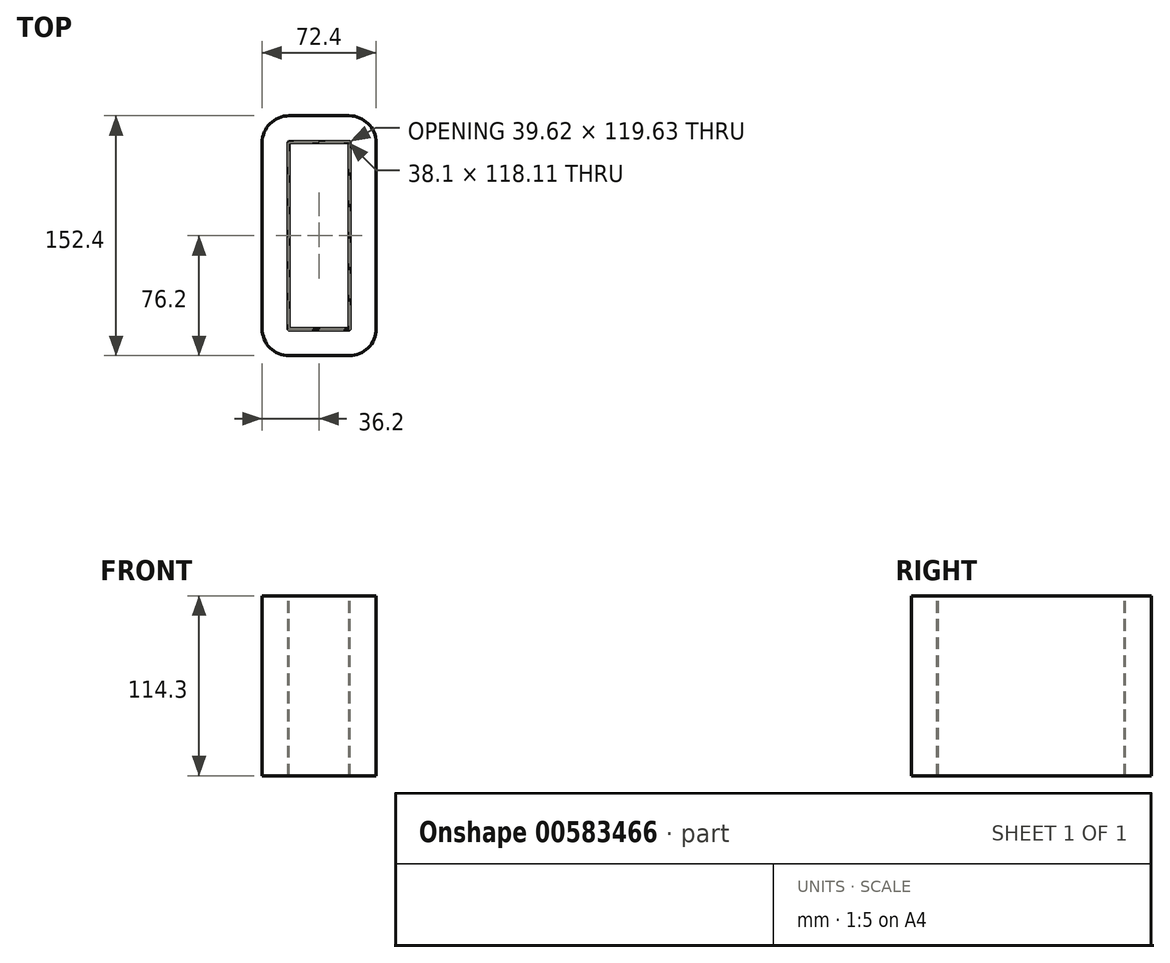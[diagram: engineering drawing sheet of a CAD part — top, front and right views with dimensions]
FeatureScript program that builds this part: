
annotation { "Feature Type Name" : "Feature", "Feature Type Description" : "" }
export const myFeature = defineFeature(function(context is Context, id is Id, definition is map)
    precondition{}
    {
        {
            assignVariable(context, id + "F0", {"name" : "Tongue", "anyValue" : 38.1 * mm});
        }
        {
            assignVariable(context, id + "F1", {"name" : "WindingWidth", "anyValue" : 114.3 * mm});
        }
        {
            assignVariable(context, id + "F2", {"name" : "CoilForm", "anyValue" : 0.76 * mm});
        }
        {
            assignVariable(context, id + "F3", {"name" : "CoilBuild", "anyValue" : 0.45 * getVariable(context, 'Tongue')});
        }
        {
            var Q0;
            Q0=qCreatedBy(makeId("Top.planeOp"),FACE);
            var sketch = newSketch(context, id + "F4", { "sketchPlane" : qUnion([Q0])});
            skLineSegment(sketch, "E0.bottom", {"start": v(-36.2, -76.2) * mm, "end": v(36.2, -76.2) * mm});
            skLineSegment(sketch, "E0.top", {"start": v(-36.2, 76.2) * mm, "end": v(36.2, 76.2) * mm});
            skLineSegment(sketch, "E0.left", {"start": v(-36.2, -76.2) * mm, "end": v(-36.2, 76.2) * mm});
            skLineSegment(sketch, "E0.right", {"start": v(36.2, -76.2) * mm, "end": v(36.2, 76.2) * mm});
            skPoint(sketch, "E0.middle", {"position": v(0, 0) * mm});
            skSolve(sketch);
        }
        {
            var Q0;
            Q0=qSketchRegion(id+"F4",true);
            extrude(context, id + "F5", {"entities" : qUnion([Q0]), "oppositeDirection" : true, "depth" : getVariable(context, 'WindingWidth')});
        }
        {
            var Q0;
            Q0=makeQuery(id+"F5.opExtrude","SWEPT_EDGE",EDGE,{"disambiguationData":[OSD([sQuery(id+"F4.wireOp",EDGE,"E0.top"),sQuery(id+"F4.wireOp",EDGE,"E0.left")])]});
            var Q1;
            Q1=makeQuery(id+"F5.opExtrude","SWEPT_EDGE",EDGE,{"disambiguationData":[OSD([sQuery(id+"F4.wireOp",EDGE,"E0.top"),sQuery(id+"F4.wireOp",EDGE,"E0.right")])]});
            var Q2;
            Q2=makeQuery(id+"F5.opExtrude","SWEPT_EDGE",EDGE,{"disambiguationData":[OSD([sQuery(id+"F4.wireOp",EDGE,"E0.bottom"),sQuery(id+"F4.wireOp",EDGE,"E0.right")])]});
            var Q3;
            Q3=makeQuery(id+"F5.opExtrude","SWEPT_EDGE",EDGE,{"disambiguationData":[OSD([sQuery(id+"F4.wireOp",EDGE,"E0.bottom"),sQuery(id+"F4.wireOp",EDGE,"E0.left")])]});
            fillet(context, id + "F6", {"entities" : qUnion([Q0, Q1, Q2, Q3]), "radius" : getVariable(context, 'CoilBuild'), "tangentPropagation" : true, "allowEdgeOverflow" : false});
        }
        {
            var Q0;
            Q0=makeQuery(id+"F5.opExtrude","CAP_FACE",FACE,{"disambiguationData":[OSD([sQuery(id+"F4.wireOp",EDGE,"E0.bottom"),sQuery(id+"F4.wireOp",EDGE,"E0.top"),sQuery(id+"F4.wireOp",EDGE,"E0.left"),sQuery(id+"F4.wireOp",EDGE,"E0.right")])],"isStart":true});
            var sketch = newSketch(context, id + "F7", { "sketchPlane" : qUnion([Q0])});
            skLineSegment(sketch, "E1.bottom", {"start": v(-19.81, -59.82) * mm, "end": v(19.81, -59.82) * mm});
            skLineSegment(sketch, "E1.top", {"start": v(-19.81, 59.82) * mm, "end": v(19.81, 59.82) * mm});
            skLineSegment(sketch, "E1.left", {"start": v(-19.81, -59.82) * mm, "end": v(-19.81, 59.82) * mm});
            skLineSegment(sketch, "E1.right", {"start": v(19.81, -59.82) * mm, "end": v(19.81, 59.82) * mm});
            skPoint(sketch, "E1.middle", {"position": v(0, 0) * mm});
            skSolve(sketch);
        }
        {
            var Q0;
            Q0=qSketchRegion(id+"F7",true);
            extrude(context, id + "F8", {"entities" : qUnion([Q0]), "operationType" : NewBodyOperationType.REMOVE, "oppositeDirection" : true, "depth" : getVariable(context, 'WindingWidth')});
        }
        {
            var Q0;
            Q0=makeQuery(id+"F5.opExtrude","CAP_FACE",FACE,{"disambiguationData":[OSD([sQuery(id+"F4.wireOp",EDGE,"E0.bottom"),sQuery(id+"F4.wireOp",EDGE,"E0.top"),sQuery(id+"F4.wireOp",EDGE,"E0.left"),sQuery(id+"F4.wireOp",EDGE,"E0.right")])],"isStart":true});
            var sketch = newSketch(context, id + "F9", { "sketchPlane" : qUnion([Q0])});
            skLineSegment(sketch, "E2.bottom", {"start": v(-19.81, -59.82) * mm, "end": v(19.81, -59.82) * mm});
            skLineSegment(sketch, "E2.top", {"start": v(-19.81, 59.82) * mm, "end": v(19.81, 59.82) * mm});
            skLineSegment(sketch, "E2.left", {"start": v(-19.81, -59.82) * mm, "end": v(-19.81, 59.82) * mm});
            skLineSegment(sketch, "E2.right", {"start": v(19.81, -59.82) * mm, "end": v(19.81, 59.82) * mm});
            skPoint(sketch, "E2.middle", {"position": v(0, 0) * mm});
            skSolve(sketch);
        }
        {
            var Q0;
            Q0=qSketchRegion(id+"F9",true);
            extrude(context, id + "F10", {"entities" : qUnion([Q0]), "oppositeDirection" : true, "depth" : getVariable(context, 'WindingWidth')});
        }
        {
            var Q0;
            Q0=makeQuery(id+"F10.opExtrude","CAP_FACE",FACE,{"disambiguationData":[OSD([sQuery(id+"F9.wireOp",EDGE,"E2.bottom"),sQuery(id+"F9.wireOp",EDGE,"E2.top"),sQuery(id+"F9.wireOp",EDGE,"E2.left"),sQuery(id+"F9.wireOp",EDGE,"E2.right")])],"isStart":true});
            var sketch = newSketch(context, id + "F11", { "sketchPlane" : qUnion([Q0])});
            skLineSegment(sketch, "E3.bottom", {"start": v(-19.05, 59.06) * mm, "end": v(19.05, 59.06) * mm});
            skLineSegment(sketch, "E3.top", {"start": v(-19.05, -59.06) * mm, "end": v(19.05, -59.06) * mm});
            skLineSegment(sketch, "E3.left", {"start": v(-19.05, 59.06) * mm, "end": v(-19.05, -59.06) * mm});
            skLineSegment(sketch, "E3.right", {"start": v(19.05, 59.06) * mm, "end": v(19.05, -59.06) * mm});
            skPoint(sketch, "E3.middle", {"position": v(0, 0) * mm});
            skSolve(sketch);
        }
        {
            var Q0;
            Q0=qSketchRegion(id+"F11",true);
            extrude(context, id + "F12", {"entities" : qUnion([Q0]), "operationType" : NewBodyOperationType.REMOVE, "oppositeDirection" : true, "depth" : getVariable(context, 'WindingWidth')});
        }
        {
            var Q0;
            Q0=makeQuery(id+"F10.opExtrude","SWEPT_EDGE",EDGE,{"disambiguationData":[OSD([sQuery(id+"F9.wireOp",EDGE,"E2.top"),sQuery(id+"F9.wireOp",EDGE,"E2.left")])]});
            var Q1;
            Q1=makeQuery(id+"F10.opExtrude","SWEPT_EDGE",EDGE,{"disambiguationData":[OSD([sQuery(id+"F9.wireOp",EDGE,"E2.top"),sQuery(id+"F9.wireOp",EDGE,"E2.right")])]});
            var Q2;
            Q2=makeQuery(id+"F10.opExtrude","SWEPT_EDGE",EDGE,{"disambiguationData":[OSD([sQuery(id+"F9.wireOp",EDGE,"E2.bottom"),sQuery(id+"F9.wireOp",EDGE,"E2.right")])]});
            var Q3;
            Q3=makeQuery(id+"F10.opExtrude","SWEPT_EDGE",EDGE,{"disambiguationData":[OSD([sQuery(id+"F9.wireOp",EDGE,"E2.bottom"),sQuery(id+"F9.wireOp",EDGE,"E2.left")])]});
            fillet(context, id + "F13", {"entities" : qUnion([Q0, Q1, Q2, Q3]), "radius" : getVariable(context, 'CoilForm'), "tangentPropagation" : true, "allowEdgeOverflow" : false});
        }
        {
            var Q0;
            Q0=makeQuery(id+"F8.boolean.opBoolean","COPY",EDGE,{"derivedFrom":makeQuery(id+"F8.opExtrude","SWEPT_EDGE",EDGE,{"disambiguationData":[OSD([sQuery(id+"F7.wireOp",EDGE,"E1.top"),sQuery(id+"F7.wireOp",EDGE,"E1.left")])]})});
            var Q1;
            Q1=makeQuery(id+"F8.boolean.opBoolean","COPY",EDGE,{"derivedFrom":makeQuery(id+"F8.opExtrude","SWEPT_EDGE",EDGE,{"disambiguationData":[OSD([sQuery(id+"F7.wireOp",EDGE,"E1.bottom"),sQuery(id+"F7.wireOp",EDGE,"E1.left")])]})});
            var Q2;
            Q2=makeQuery(id+"F8.boolean.opBoolean","COPY",EDGE,{"derivedFrom":makeQuery(id+"F8.opExtrude","SWEPT_EDGE",EDGE,{"disambiguationData":[OSD([sQuery(id+"F7.wireOp",EDGE,"E1.bottom"),sQuery(id+"F7.wireOp",EDGE,"E1.right")])]})});
            var Q3;
            Q3=makeQuery(id+"F8.boolean.opBoolean","COPY",EDGE,{"derivedFrom":makeQuery(id+"F8.opExtrude","SWEPT_EDGE",EDGE,{"disambiguationData":[OSD([sQuery(id+"F7.wireOp",EDGE,"E1.top"),sQuery(id+"F7.wireOp",EDGE,"E1.right")])]})});
            fillet(context, id + "F14", {"entities" : qUnion([Q0, Q1, Q2, Q3]), "radius" : getVariable(context, 'CoilForm'), "tangentPropagation" : true, "allowEdgeOverflow" : false});
        }
    });
